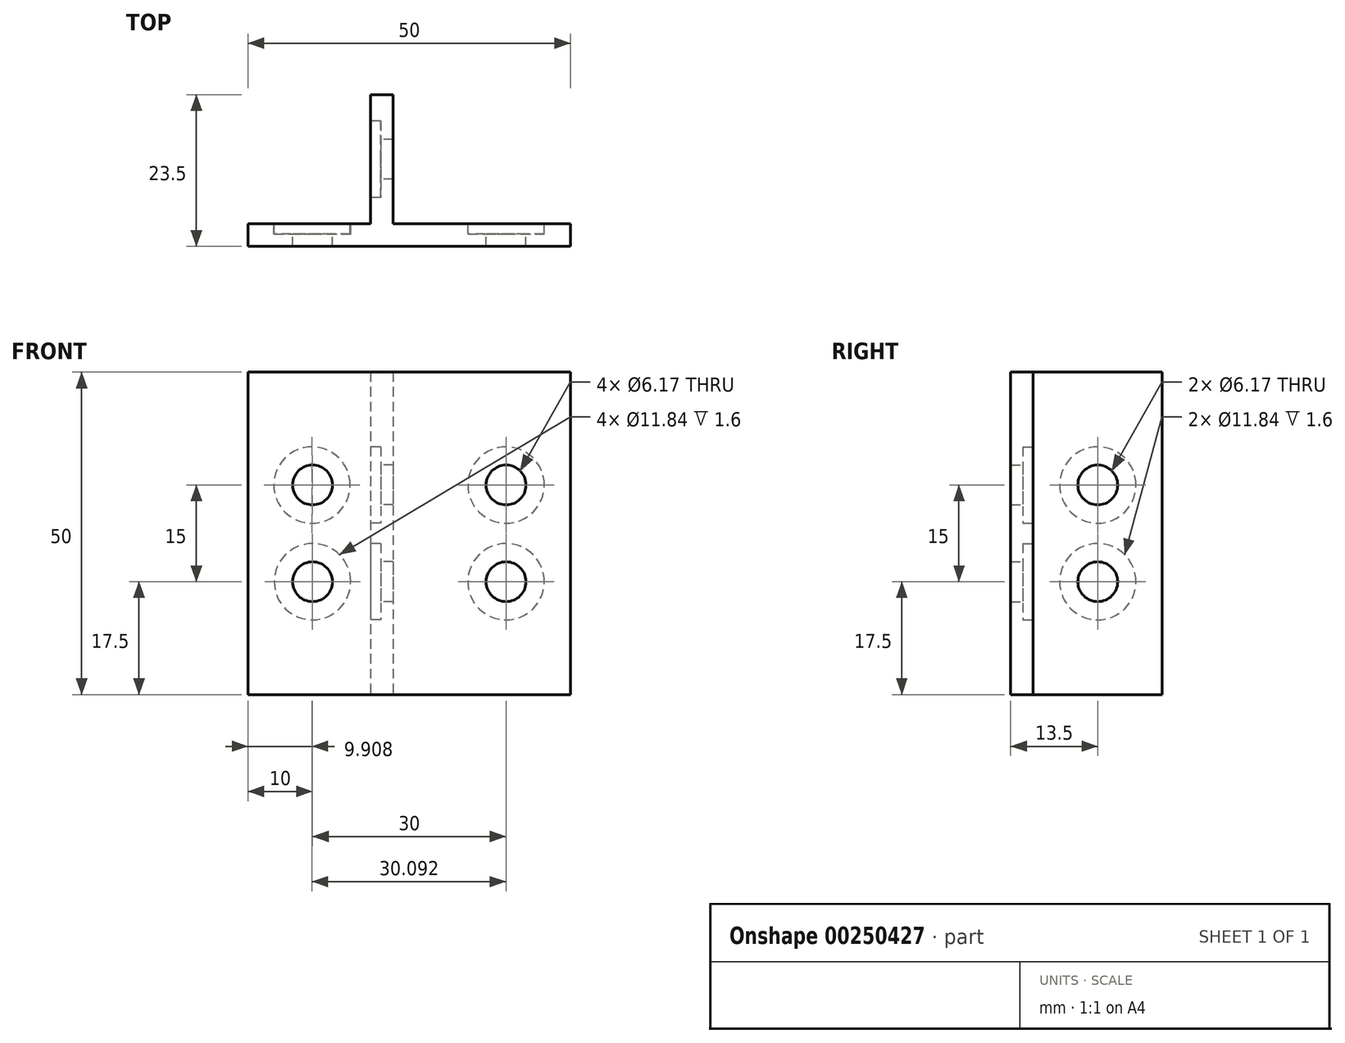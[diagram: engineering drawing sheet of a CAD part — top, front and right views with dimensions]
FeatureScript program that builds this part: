
annotation { "Feature Type Name" : "Feature", "Feature Type Description" : "" }
export const myFeature = defineFeature(function(context is Context, id is Id, definition is map)
    precondition{}
    {
        {
            var Q0;
            Q0=qCreatedBy(makeId("Front.planeOp"),FACE);
            var sketch = newSketch(context, id + "F0", { "sketchPlane" : qUnion([Q0])});
            skLineSegment(sketch, "E0.bottom", {"start": v(25, -25) * mm, "end": v(-25, -25) * mm});
            skLineSegment(sketch, "E0.top", {"start": v(25, 25) * mm, "end": v(-25, 25) * mm});
            skLineSegment(sketch, "E0.left", {"start": v(25, -25) * mm, "end": v(25, 25) * mm});
            skLineSegment(sketch, "E0.right", {"start": v(-25, -25) * mm, "end": v(-25, 25) * mm});
            skPoint(sketch, "E0.middle", {"position": v(0, 0) * mm});
            skSolve(sketch);
        }
        {
            var Q0;
            Q0 = qSketchRegion(id + "F0", true);
            extrude(context, id + "F1", {"entities" : qUnion([Q0]), "depth" : 3.5 * mm});
        }
        {
            var Q0;
            Q0=qCreatedBy(makeId("Top.planeOp"),FACE);
            var sketch = newSketch(context, id + "F2", { "sketchPlane" : qUnion([Q0])});
            skLineSegment(sketch, "E1.bottom", {"start": v(-2.5, 0) * mm, "end": v(-6, 0) * mm});
            skLineSegment(sketch, "E1.top", {"start": v(-2.5, 20) * mm, "end": v(-6, 20) * mm});
            skLineSegment(sketch, "E1.left", {"start": v(-2.5, 0) * mm, "end": v(-2.5, 20) * mm});
            skLineSegment(sketch, "E1.right", {"start": v(-6, 0) * mm, "end": v(-6, 20) * mm});
            skSolve(sketch);
        }
        {
            var Q0;
            Q0 = qSketchRegion(id + "F2", true);
            extrude(context, id + "F3", {"entities" : qUnion([Q0]), "operationType" : NewBodyOperationType.ADD, "endBound" : BoundingType.SYMMETRIC, "depth" : 50 * mm});
        }
        {
            var Q0;
            Q0=makeQuery(id+"F3.opExtrude","SWEPT_FACE",FACE,{"disambiguationData":[OSD([sQuery(id+"F2.wireOp",EDGE,"E1.right")])]});
            var sketch = newSketch(context, id + "F4", { "sketchPlane" : qUnion([Q0])});
            skCircle(sketch, "E2", {"center": v(-10, 7.5) * mm, "radius": 3.09 * mm});
            skCircle(sketch, "E3", {"center": v(-10, -7.5) * mm, "radius": 3.09 * mm});
            skLineSegment(sketch, "E4", {"start": v(-10, 7.5) * mm, "end": v(-10, 0) * mm});
            skLineSegment(sketch, "E5", {"start": v(-10, 0) * mm, "end": v(-10, -7.5) * mm});
            skLineSegment(sketch, "E6", {"start": v(-10, -7.5) * mm, "end": v(0, -7.5) * mm});
            skLineSegment(sketch, "E7", {"start": v(-10, 7.5) * mm, "end": v(0, 7.5) * mm});
            skSolve(sketch);
        }
        {
            var Q0;
            Q0 = qSketchRegion(id + "F4", true);
            extrude(context, id + "F5", {"entities" : qUnion([Q0]), "operationType" : NewBodyOperationType.REMOVE, "oppositeDirection" : true, "depth" : 25 * mm});
        }
        {
            var Q0;
            Q0=makeQuery(id+"F3.opExtrude","SWEPT_FACE",FACE,{"disambiguationData":[OSD([sQuery(id+"F2.wireOp",EDGE,"E1.right")])]});
            var sketch = newSketch(context, id + "F6", { "sketchPlane" : qUnion([Q0])});
            skCircle(sketch, "E8", {"center": v(-10, 7.5) * mm, "radius": 5.92 * mm});
            skCircle(sketch, "E9", {"center": v(-10, -7.5) * mm, "radius": 5.92 * mm});
            skSolve(sketch);
        }
        {
            var Q0;
            Q0 = qSketchRegion(id + "F6", true);
            extrude(context, id + "F7", {"entities" : qUnion([Q0]), "operationType" : NewBodyOperationType.REMOVE, "oppositeDirection" : true, "depth" : 1.6 * mm});
        }
        {
            var Q0;
            {var subQ4=sQuery(id+"F0.wireOp",EDGE,"E0.left");var subQ5=sQuery(id+"F0.wireOp",EDGE,"E0.top");var subQ6=sQuery(id+"F0.wireOp",EDGE,"E0.bottom");Q0=makeQuery(id+"F3.boolean.opBoolean","SPLIT",FACE,{"disambiguationData":[TD([makeQuery(id+"F1.opExtrude","SWEPT_FACE",FACE,{"disambiguationData":[OSD([subQ4])]})])],"derivedFrom":makeQuery(id+"F1.opExtrude","CAP_FACE",FACE,{"disambiguationData":[OSD([subQ6,subQ5,subQ4,sQuery(id+"F0.wireOp",EDGE,"E0.right")])],"isStart":true})});}
            var sketch = newSketch(context, id + "F8", { "sketchPlane" : qUnion([Q0])});
            skCircle(sketch, "E10", {"center": v(-15, 7.5) * mm, "radius": 3.09 * mm});
            skCircle(sketch, "E11", {"center": v(-15, -7.5) * mm, "radius": 3.09 * mm});
            skCircle(sketch, "E12", {"center": v(15, 7.5) * mm, "radius": 3.09 * mm});
            skCircle(sketch, "E13", {"center": v(15, -7.5) * mm, "radius": 3.09 * mm});
            skLineSegment(sketch, "E14", {"start": v(-15, 7.5) * mm, "end": v(-15, 0) * mm, "construction": true});
            skPoint(sketch, "E14.endSnap0", {"position": v(-25, 0) * mm});
            skLineSegment(sketch, "E15", {"start": v(-15, 0) * mm, "end": v(-15, -7.5) * mm, "construction": true});
            skLineSegment(sketch, "E16", {"start": v(-15, -7.5) * mm, "end": v(0, -7.5) * mm, "construction": true});
            skLineSegment(sketch, "E17", {"start": v(0, -7.5) * mm, "end": v(15, -7.5) * mm, "construction": true});
            skLineSegment(sketch, "E18", {"start": v(15, -7.5) * mm, "end": v(15, 0) * mm, "construction": true});
            skLineSegment(sketch, "E19", {"start": v(15, 0) * mm, "end": v(15, 7.5) * mm, "construction": true});
            skLineSegment(sketch, "E20", {"start": v(-15, 7.5) * mm, "end": v(0, 7.5) * mm, "construction": true});
            skLineSegment(sketch, "E21", {"start": v(0, 7.5) * mm, "end": v(15, 7.5) * mm, "construction": true});
            skSolve(sketch);
        }
        {
            var Q0;
            Q0 = qSketchRegion(id + "F8", true);
            extrude(context, id + "F9", {"entities" : qUnion([Q0]), "operationType" : NewBodyOperationType.REMOVE, "oppositeDirection" : true, "depth" : 25 * mm});
        }
        {
            var Q0;
            {var subQ4=sQuery(id+"F0.wireOp",EDGE,"E0.left");var subQ5=sQuery(id+"F0.wireOp",EDGE,"E0.top");var subQ6=sQuery(id+"F0.wireOp",EDGE,"E0.bottom");Q0=makeQuery(id+"F3.boolean.opBoolean","SPLIT",FACE,{"disambiguationData":[TD([makeQuery(id+"F1.opExtrude","SWEPT_FACE",FACE,{"disambiguationData":[OSD([subQ4])]})])],"derivedFrom":makeQuery(id+"F1.opExtrude","CAP_FACE",FACE,{"disambiguationData":[OSD([subQ6,subQ5,subQ4,sQuery(id+"F0.wireOp",EDGE,"E0.right")])],"isStart":true})});}
            var sketch = newSketch(context, id + "F10", { "sketchPlane" : qUnion([Q0])});
            skCircle(sketch, "E22", {"center": v(-15, 7.5) * mm, "radius": 5.92 * mm});
            skCircle(sketch, "E23", {"center": v(-15, -7.5) * mm, "radius": 5.92 * mm});
            skCircle(sketch, "E24", {"center": v(15.1, 7.5) * mm, "radius": 5.92 * mm});
            skCircle(sketch, "E25", {"center": v(15, -7.5) * mm, "radius": 5.92 * mm});
            skSolve(sketch);
        }
        {
            var Q0;
            Q0 = qSketchRegion(id + "F10", true);
            extrude(context, id + "F11", {"entities" : qUnion([Q0]), "operationType" : NewBodyOperationType.REMOVE, "oppositeDirection" : true, "depth" : 1.6 * mm});
        }
    });
